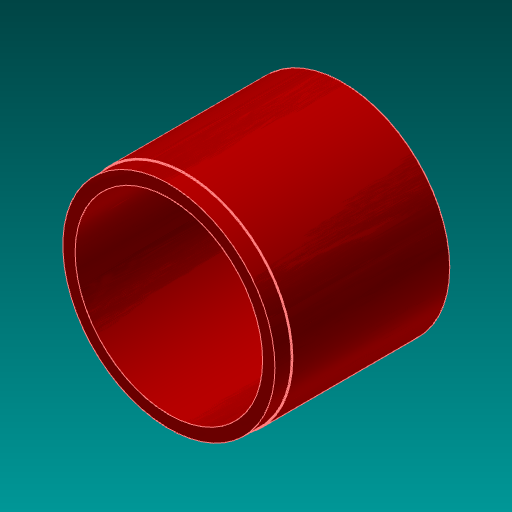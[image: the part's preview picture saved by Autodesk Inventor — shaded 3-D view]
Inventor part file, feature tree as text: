
AUTODESK INVENTOR PART (.ipt)
format: ipt  version: 2017.3 (Build 213257000, 257)  size: 162,304 bytes
history: native  units: in
note: dims shown in document units (in); Inventor stores cm internally (conversion verified against a paired STEP export)
features: extrude x2, sketch x2, fillet x1, chamfer x1
ambient origin geometry x8: Origin, YZ Plane, XZ Plane, XY Plane, X Axis, Y Axis, Z Axis, Center Point
bodies: Solid1 (feature_tree)
feature tree (6):
  extrude  "Extrusion1"  Depth=12.73in
  extrude  "Extrusion2"  Depth=0.0312in
  fillet  "Fillet1"  Radius=1.0in
  chamfer  "Chamfer1"  Distance=0.0312in
  sketch  "Sketch1"  dims[d0=11.1417in d1=12.73in]
  sketch  "Sketch2"  dims[d2=10.3543in d3=0.0in d4=12.605in d5=1.0in d6=0.0in d10=0.0312in d11=0.0312in d12=0.125in d13=45.0deg]
